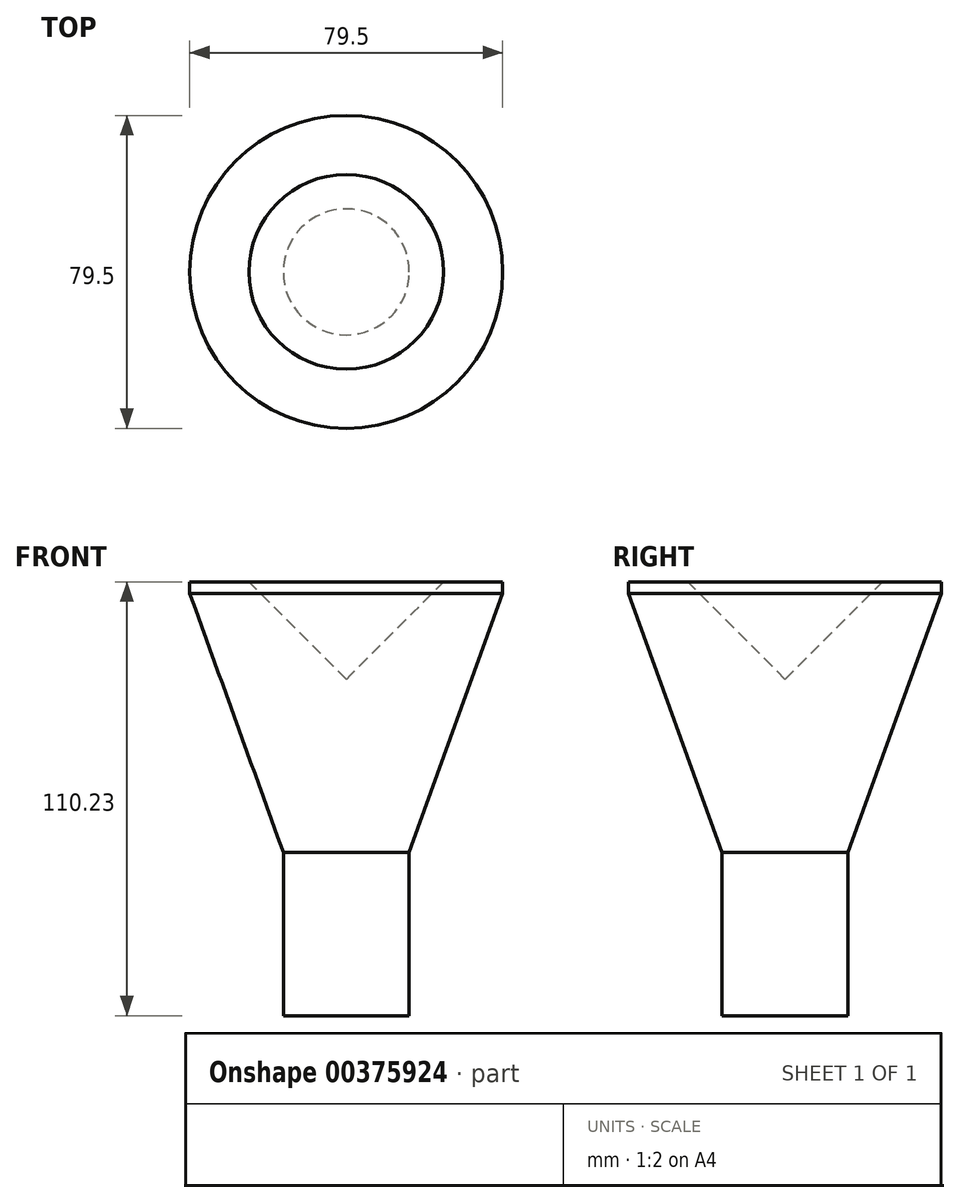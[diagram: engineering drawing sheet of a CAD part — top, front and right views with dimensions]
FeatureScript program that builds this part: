
annotation { "Feature Type Name" : "Feature", "Feature Type Description" : "" }
export const myFeature = defineFeature(function(context is Context, id is Id, definition is map)
    precondition{}
    {
        {
            var Q0;
            Q0=qCreatedBy(makeId("Right.planeOp"),FACE);
            var sketch = newSketch(context, id + "F0", { "sketchPlane" : qUnion([Q0])});
            skLineSegment(sketch, "E0", {"start": v(0, 0) * mm, "end": v(0, 44) * mm});
            skLineSegment(sketch, "E1", {"start": v(0, 44) * mm, "end": v(24.75, 68.75) * mm});
            skLineSegment(sketch, "E2", {"start": v(39.75, 68.75) * mm, "end": v(24.75, 68.75) * mm});
            skLineSegment(sketch, "E3", {"start": v(39.75, 65.75) * mm, "end": v(39.75, 68.75) * mm});
            skLineSegment(sketch, "E4", {"start": v(39.75, 65.75) * mm, "end": v(16, 0) * mm});
            skLineSegment(sketch, "E5", {"start": v(16, 0) * mm, "end": v(0, 0) * mm});
            skLineSegment(sketch, "E6", {"start": v(0, -58.91) * mm, "end": v(0, 0) * mm, "construction": true});
            skSolve(sketch);
        }
        {
            var Q0;
            Q0=makeQuery(id+"F0.imprint","IMPRINT",FACE,{"disambiguationData":[TD([[makeQuery(id+"F0.imprint","IMPRINT",EDGE,{"derivedFrom":sQuery(id+"F0.wireOp",EDGE,"E0")}),-1.0]])]});
            var Q1;
            Q1=sQuery(id+"F0.wireOp",EDGE,"E6");
            revolve(context, id + "F1", {"entities" : qUnion([Q0]), "axis" : qUnion([Q1]), "revolveType" : RevolveType.FULL});
        }
        {
            var Q0;
            Q0=makeQuery(id+"F1.opRevolve","SWEPT_FACE",FACE,{"disambiguationData":[OSD([sQuery(id+"F0.wireOp",EDGE,"E5")])]});
            var sketch = newSketch(context, id + "F2", { "sketchPlane" : qUnion([Q0])});
            skCircle(sketch, "E7.0", {"center": v(0, 0) * mm, "radius": 16 * mm});
            skSolve(sketch);
        }
        {
            var Q0;
            Q0 = qSketchRegion(id + "F2", true);
            extrude(context, id + "F3", {"entities" : qUnion([Q0]), "operationType" : NewBodyOperationType.ADD, "depth" : 41.48 * mm});
        }
    });
